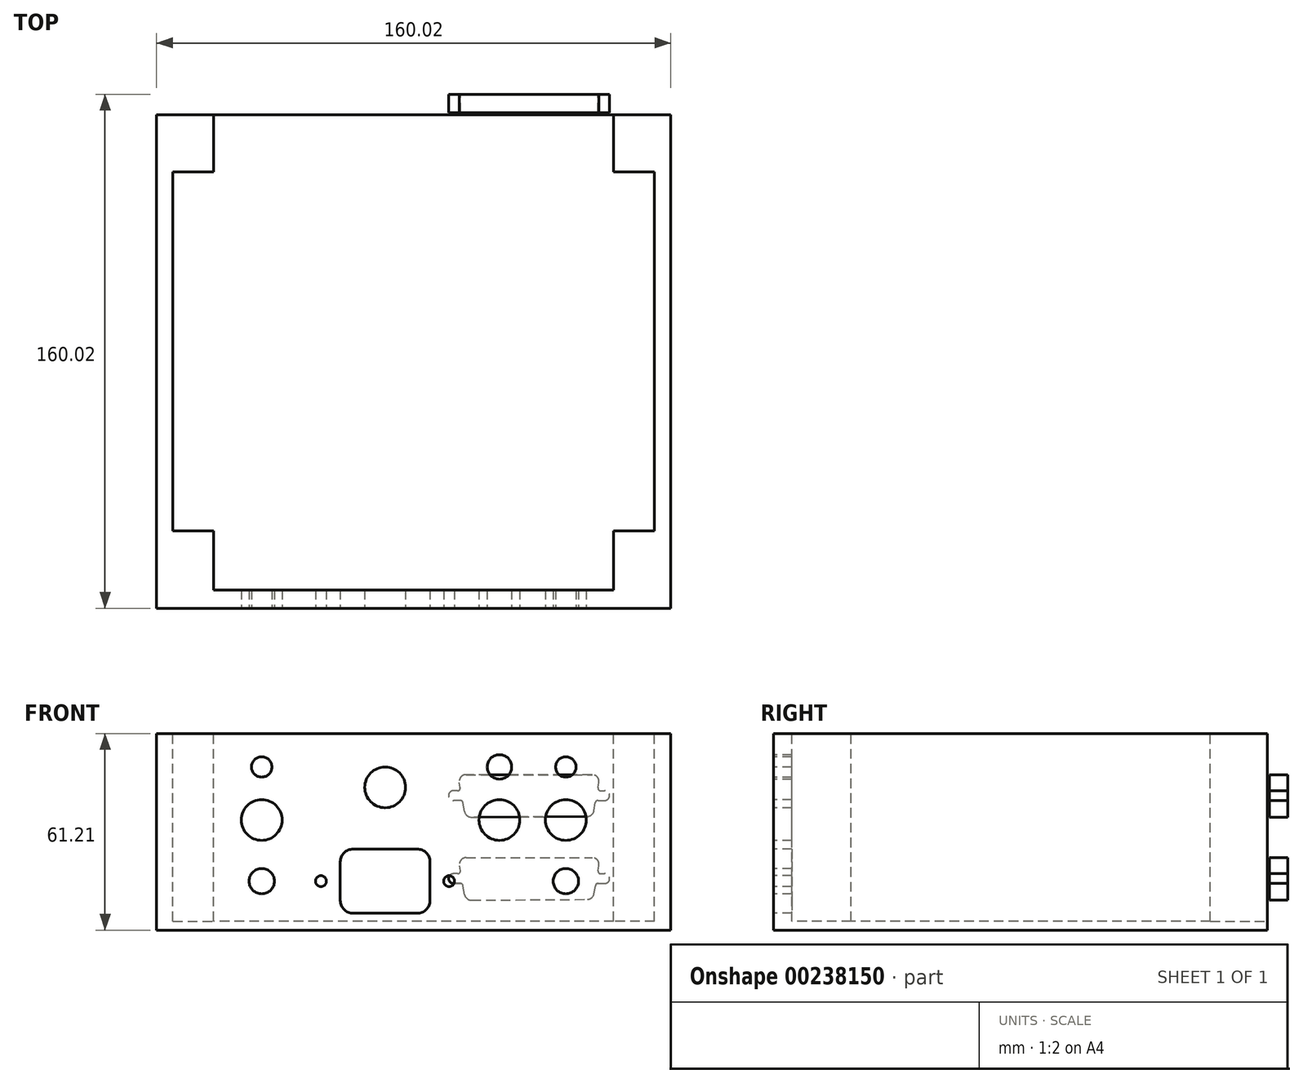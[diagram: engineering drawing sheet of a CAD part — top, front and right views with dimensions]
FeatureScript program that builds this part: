
annotation { "Feature Type Name" : "Feature", "Feature Type Description" : "" }
export const myFeature = defineFeature(function(context is Context, id is Id, definition is map)
    precondition{}
    {
        {
            var Q0;
            Q0=qCreatedBy(makeId("Top.planeOp"),FACE);
            var sketch = newSketch(context, id + "F0", { "sketchPlane" : qUnion([Q0])});
            skLineSegment(sketch, "E0.bottom", {"start": v(0, 0) * mm, "end": v(160.02, 0) * mm});
            skLineSegment(sketch, "E0.top", {"start": v(0, 160.02) * mm, "end": v(160.02, 160.02) * mm});
            skLineSegment(sketch, "E0.left", {"start": v(0, 0) * mm, "end": v(0, 160.02) * mm});
            skLineSegment(sketch, "E0.right", {"start": v(160.02, 0) * mm, "end": v(160.02, 160.02) * mm});
            skSolve(sketch);
        }
        {
            var Q0;
            Q0=makeQuery(id+"F0.imprint","IMPRINT",FACE,{"disambiguationData":[TD([[makeQuery(id+"F0.imprint","IMPRINT",EDGE,{"derivedFrom":sQuery(id+"F0.wireOp",EDGE,"E0.bottom")}),1.0]])]});
            extrude(context, id + "F1", {"entities" : qUnion([Q0]), "oppositeDirection" : true, "depth" : 61.2 * mm});
        }
        {
            var Q0;
            Q0=makeQuery(id+"F1.opExtrude","CAP_FACE",FACE,{"disambiguationData":[OSD([sQuery(id+"F0.wireOp",EDGE,"E0.bottom"),sQuery(id+"F0.wireOp",EDGE,"E0.top"),sQuery(id+"F0.wireOp",EDGE,"E0.left"),sQuery(id+"F0.wireOp",EDGE,"E0.right")])],"isStart":true});
            var sketch = newSketch(context, id + "F2", { "sketchPlane" : qUnion([Q0])});
            skLineSegment(sketch, "E1.bottom", {"start": v(5.08, 154.3) * mm, "end": v(154.94, 154.3) * mm});
            skLineSegment(sketch, "E1.top", {"start": v(5.08, 5.71) * mm, "end": v(154.94, 5.72) * mm});
            skLineSegment(sketch, "E1.left", {"start": v(5.08, 154.3) * mm, "end": v(5.08, 5.71) * mm});
            skLineSegment(sketch, "E1.right", {"start": v(154.94, 154.3) * mm, "end": v(154.94, 5.72) * mm});
            skLineSegment(sketch, "E2", {"start": v(5.08, 24.13) * mm, "end": v(17.78, 24.13) * mm});
            skLineSegment(sketch, "E3", {"start": v(17.78, 24.13) * mm, "end": v(17.78, 5.71) * mm});
            skLineSegment(sketch, "E4", {"start": v(154.94, 24.13) * mm, "end": v(142.24, 24.13) * mm});
            skLineSegment(sketch, "E5", {"start": v(142.24, 24.13) * mm, "end": v(142.24, 5.72) * mm});
            skLineSegment(sketch, "E6", {"start": v(5.08, 135.9) * mm, "end": v(17.78, 135.9) * mm});
            skLineSegment(sketch, "E7", {"start": v(17.78, 135.9) * mm, "end": v(17.78, 154.3) * mm});
            skLineSegment(sketch, "E8", {"start": v(154.94, 135.9) * mm, "end": v(142.24, 135.9) * mm});
            skLineSegment(sketch, "E9", {"start": v(142.24, 135.9) * mm, "end": v(142.24, 154.3) * mm});
            skSolve(sketch);
        }
        {
            var Q0;
            {var subQ3=sQuery(id+"F2.wireOp",EDGE,"E2");Q0=makeQuery(id+"F2.imprint","IMPRINT",FACE,{"disambiguationData":[TD([[makeQuery(id+"F2.imprint","IMPRINT",EDGE,{"derivedFrom":subQ3}),1.0]])]});}
            extrude(context, id + "F3", {"entities" : qUnion([Q0]), "operationType" : NewBodyOperationType.REMOVE, "oppositeDirection" : true, "depth" : 58.42 * mm});
        }
        {
            var Q0;
            Q0=makeQuery(id+"F1.opExtrude","SWEPT_FACE",FACE,{"disambiguationData":[OSD([sQuery(id+"F0.wireOp",EDGE,"E0.bottom")])]});
            var sketch = newSketch(context, id + "F4", { "sketchPlane" : qUnion([Q0])});
            skCircle(sketch, "E10", {"center": v(32.7, -45.97) * mm, "radius": 3.94 * mm});
            skCircle(sketch, "E11.1.0.0", {"center": v(127.34, -45.97) * mm, "radius": 3.94 * mm});
            skLineSegment(sketch, "E11.direction1", {"start": v(32.7, -45.97) * mm, "end": v(127.34, -45.97) * mm, "construction": true});
            skSolve(sketch);
        }
        {
            var Q0;
            Q0=makeQuery(id+"F4.imprint","IMPRINT",FACE,{"disambiguationData":[TD([[makeQuery(id+"F4.imprint","IMPRINT",EDGE,{"derivedFrom":sQuery(id+"F4.wireOp",EDGE,"E10")}),1.0]])]});
            var Q1;
            Q1=makeQuery(id+"F4.imprint","IMPRINT",FACE,{"disambiguationData":[TD([[makeQuery(id+"F4.imprint","IMPRINT",EDGE,{"derivedFrom":sQuery(id+"F4.wireOp",EDGE,"E11.1.0.0")}),1.0]])]});
            extrude(context, id + "F5", {"entities" : qUnion([Q0, Q1]), "operationType" : NewBodyOperationType.REMOVE, "oppositeDirection" : true, "depth" : 6.35 * mm});
        }
        {
            var Q0;
            Q0=makeQuery(id+"F1.opExtrude","SWEPT_FACE",FACE,{"disambiguationData":[OSD([sQuery(id+"F0.wireOp",EDGE,"E0.bottom")])]});
            var sketch = newSketch(context, id + "F6", { "sketchPlane" : qUnion([Q0])});
            skLineSegment(sketch, "E12.bottom", {"start": v(61.14, -35.98) * mm, "end": v(81.1, -35.98) * mm});
            skLineSegment(sketch, "E12.top", {"start": v(61.14, -55.97) * mm, "end": v(81.1, -55.97) * mm});
            skLineSegment(sketch, "E12.left", {"start": v(57.15, -39.97) * mm, "end": v(57.15, -51.98) * mm});
            skLineSegment(sketch, "E12.right", {"start": v(85.1, -39.97) * mm, "end": v(85.1, -51.98) * mm});
            skPoint(sketch, "E13.visualSharp", {"position": v(57.15, -35.98) * mm});
            skArc(sketch, "E13.filletArc", {"start": v(61.14, -35.98) * mm, "mid": v(58.32, -37.15) * mm, "end": v(57.15, -39.97) * mm});
            skPoint(sketch, "E14.visualSharp", {"position": v(57.15, -55.97) * mm});
            skArc(sketch, "E14.filletArc", {"start": v(57.15, -51.98) * mm, "mid": v(58.32, -54.8) * mm, "end": v(61.14, -55.97) * mm});
            skPoint(sketch, "E15.visualSharp", {"position": v(85.1, -55.97) * mm});
            skArc(sketch, "E15.filletArc", {"start": v(81.1, -55.97) * mm, "mid": v(83.92, -54.8) * mm, "end": v(85.1, -51.98) * mm});
            skPoint(sketch, "E16.visualSharp", {"position": v(85.1, -35.98) * mm});
            skArc(sketch, "E16.filletArc", {"start": v(85.1, -39.97) * mm, "mid": v(83.92, -37.15) * mm, "end": v(81.1, -35.98) * mm});
            skSolve(sketch);
        }
        {
            var Q0;
            Q0=makeQuery(id+"F6.imprint","IMPRINT",FACE,{"disambiguationData":[TD([[makeQuery(id+"F6.imprint","IMPRINT",EDGE,{"derivedFrom":sQuery(id+"F6.wireOp",EDGE,"E12.bottom")}),-1.0]])]});
            extrude(context, id + "F7", {"entities" : qUnion([Q0]), "operationType" : NewBodyOperationType.REMOVE, "oppositeDirection" : true, "depth" : 6.35 * mm});
        }
        {
            var Q0;
            Q0=makeQuery(id+"F1.opExtrude","SWEPT_FACE",FACE,{"disambiguationData":[OSD([sQuery(id+"F0.wireOp",EDGE,"E0.bottom")])]});
            var sketch = newSketch(context, id + "F8", { "sketchPlane" : qUnion([Q0])});
            skCircle(sketch, "E17", {"center": v(51.13, -45.97) * mm, "radius": 1.7 * mm});
            skCircle(sketch, "E18.1.0.0", {"center": v(91, -45.97) * mm, "radius": 1.7 * mm});
            skLineSegment(sketch, "E18.direction1", {"start": v(51.13, -45.97) * mm, "end": v(91, -45.97) * mm, "construction": true});
            skSolve(sketch);
        }
        {
            var Q0;
            Q0=makeQuery(id+"F8.imprint","IMPRINT",FACE,{"disambiguationData":[TD([[makeQuery(id+"F8.imprint","IMPRINT",EDGE,{"derivedFrom":sQuery(id+"F8.wireOp",EDGE,"E17")}),1.0]])]});
            var Q1;
            Q1=makeQuery(id+"F8.imprint","IMPRINT",FACE,{"disambiguationData":[TD([[makeQuery(id+"F8.imprint","IMPRINT",EDGE,{"derivedFrom":sQuery(id+"F8.wireOp",EDGE,"E18.1.0.0")}),1.0]])]});
            extrude(context, id + "F9", {"entities" : qUnion([Q0, Q1]), "operationType" : NewBodyOperationType.REMOVE, "oppositeDirection" : true, "depth" : 6.35 * mm});
        }
        {
            var Q0;
            Q0=makeQuery(id+"F1.opExtrude","SWEPT_FACE",FACE,{"disambiguationData":[OSD([sQuery(id+"F0.wireOp",EDGE,"E0.bottom")])]});
            var sketch = newSketch(context, id + "F10", { "sketchPlane" : qUnion([Q0])});
            skLineSegment(sketch, "E19.bottom", {"start": v(46.35, -34.98) * mm, "end": v(95.88, -34.98) * mm});
            skLineSegment(sketch, "E19.top", {"start": v(46.35, -56.97) * mm, "end": v(95.88, -56.97) * mm});
            skLineSegment(sketch, "E19.left", {"start": v(46.35, -34.98) * mm, "end": v(46.35, -56.97) * mm});
            skLineSegment(sketch, "E19.right", {"start": v(95.88, -34.98) * mm, "end": v(95.88, -56.97) * mm});
            skSolve(sketch);
        }
        {
            var Q0;
            Q0=makeQuery(id+"F10.imprint","IMPRINT",FACE,{"disambiguationData":[TD([[makeQuery(id+"F10.imprint","IMPRINT",EDGE,{"derivedFrom":sQuery(id+"F10.wireOp",EDGE,"E19.bottom")}),1.0]])]});
            var sketch = newSketch(context, id + "F11", { "sketchPlane" : qUnion([Q0])});
            skCircle(sketch, "E20", {"center": v(32.69, -26.92) * mm, "radius": 6.35 * mm});
            skCircle(sketch, "E21.1.0.0", {"center": v(127.33, -26.92) * mm, "radius": 6.35 * mm});
            skLineSegment(sketch, "E21.direction1", {"start": v(32.69, -26.92) * mm, "end": v(127.33, -26.92) * mm, "construction": true});
            skSolve(sketch);
        }
        {
            var Q0;
            Q0=makeQuery(id+"F11.imprint","IMPRINT",FACE,{"disambiguationData":[TD([[makeQuery(id+"F11.imprint","IMPRINT",EDGE,{"derivedFrom":sQuery(id+"F11.wireOp",EDGE,"E20")}),1.0]])]});
            var Q1;
            Q1=makeQuery(id+"F11.imprint","IMPRINT",FACE,{"disambiguationData":[TD([[makeQuery(id+"F11.imprint","IMPRINT",EDGE,{"derivedFrom":sQuery(id+"F11.wireOp",EDGE,"E21.1.0.0")}),1.0]])]});
            extrude(context, id + "F12", {"entities" : qUnion([Q0, Q1]), "operationType" : NewBodyOperationType.REMOVE, "oppositeDirection" : true, "depth" : 6.35 * mm});
        }
        {
            var Q0;
            Q0=makeQuery(id+"F10.imprint","IMPRINT",FACE,{"disambiguationData":[TD([[makeQuery(id+"F10.imprint","IMPRINT",EDGE,{"derivedFrom":sQuery(id+"F10.wireOp",EDGE,"E19.bottom")}),1.0]])]});
            var sketch = newSketch(context, id + "F13", { "sketchPlane" : qUnion([Q0])});
            skCircle(sketch, "E22", {"center": v(32.69, -10.41) * mm, "radius": 3.18 * mm});
            skCircle(sketch, "E23.1.0.0", {"center": v(127.33, -10.41) * mm, "radius": 3.18 * mm});
            skLineSegment(sketch, "E23.direction1", {"start": v(32.69, -10.41) * mm, "end": v(127.33, -10.41) * mm, "construction": true});
            skSolve(sketch);
        }
        {
            var Q0;
            Q0=qSketchRegion(id+"F13",true);
            extrude(context, id + "F14", {"entities" : qUnion([Q0]), "operationType" : NewBodyOperationType.REMOVE, "oppositeDirection" : true, "depth" : 6.35 * mm});
        }
        {
            var Q0;
            Q0=makeQuery(id+"F10.imprint","IMPRINT",FACE,{"disambiguationData":[TD([[makeQuery(id+"F10.imprint","IMPRINT",EDGE,{"derivedFrom":sQuery(id+"F10.wireOp",EDGE,"E19.bottom")}),1.0]])]});
            var sketch = newSketch(context, id + "F15", { "sketchPlane" : qUnion([Q0])});
            skCircle(sketch, "E24", {"center": v(71.12, -16.76) * mm, "radius": 6.35 * mm});
            skSolve(sketch);
        }
        {
            var Q0;
            Q0=makeQuery(id+"F15.imprint","IMPRINT",FACE,{"disambiguationData":[TD([[makeQuery(id+"F15.imprint","IMPRINT",EDGE,{"derivedFrom":sQuery(id+"F15.wireOp",EDGE,"E24")}),1.0]])]});
            extrude(context, id + "F16", {"entities" : qUnion([Q0]), "operationType" : NewBodyOperationType.REMOVE, "oppositeDirection" : true, "depth" : 6.35 * mm});
        }
        {
            var Q0;
            Q0=makeQuery(id+"F10.imprint","IMPRINT",FACE,{"disambiguationData":[TD([[makeQuery(id+"F10.imprint","IMPRINT",EDGE,{"derivedFrom":sQuery(id+"F10.wireOp",EDGE,"E19.bottom")}),1.0]])]});
            var sketch = newSketch(context, id + "F17", { "sketchPlane" : qUnion([Q0])});
            skCircle(sketch, "E25", {"center": v(106.68, -26.92) * mm, "radius": 6.35 * mm});
            skSolve(sketch);
        }
        {
            var Q0;
            Q0=qSketchRegion(id+"F17",true);
            extrude(context, id + "F18", {"entities" : qUnion([Q0]), "operationType" : NewBodyOperationType.REMOVE, "oppositeDirection" : true, "depth" : 6.35 * mm});
        }
        {
            var Q0;
            Q0=makeQuery(id+"F10.imprint","IMPRINT",FACE,{"disambiguationData":[TD([[makeQuery(id+"F10.imprint","IMPRINT",EDGE,{"derivedFrom":sQuery(id+"F10.wireOp",EDGE,"E19.bottom")}),1.0]])]});
            var sketch = newSketch(context, id + "F19", { "sketchPlane" : qUnion([Q0])});
            skCircle(sketch, "E26", {"center": v(106.68, -10.41) * mm, "radius": 3.81 * mm});
            skSolve(sketch);
        }
        {
            var Q0;
            Q0=qSketchRegion(id+"F19",true);
            extrude(context, id + "F20", {"entities" : qUnion([Q0]), "operationType" : NewBodyOperationType.REMOVE, "oppositeDirection" : true, "depth" : 6.35 * mm});
        }
        {
            var Q0;
            Q0=makeQuery(id+"F1.opExtrude","SWEPT_FACE",FACE,{"disambiguationData":[OSD([sQuery(id+"F0.wireOp",EDGE,"E0.top")])]});
            var sketch = newSketch(context, id + "F21", { "sketchPlane" : qUnion([Q0])});
            skSolve(sketch);
        }
        {
            var Q0;
            {var subQ0=sQuery(id+"F0.wireOp",EDGE,"E0.top");Q0=makeQuery(id+"F21.imprint","IMPRINT",FACE,{"disambiguationData":[TD([[makeQuery(id+"F21.imprint","IMPRINT",EDGE,{"derivedFrom":makeQuery(id+"F1.opExtrude","CAP_EDGE",EDGE,{"disambiguationData":[OSD([subQ0])],"isStart":true})}),1.0]])]});}
            var sketch = newSketch(context, id + "F22", { "sketchPlane" : qUnion([Q0])});
            skLineSegment(sketch, "E27", {"start": v(-140.97, -45.17) * mm, "end": v(-139.45, -45.17) * mm, "construction": true});
            skArc(sketch, "E28", {"start": v(-139.45, -46.7) * mm, "mid": v(-140.97, -45.17) * mm, "end": v(-139.45, -43.65) * mm});
            skLineSegment(sketch, "E29", {"start": v(-90.88, -45.17) * mm, "end": v(-92.4, -45.17) * mm, "construction": true});
            skArc(sketch, "E30", {"start": v(-92.4, -43.65) * mm, "mid": v(-90.88, -45.17) * mm, "end": v(-92.4, -46.7) * mm});
            skLineSegment(sketch, "E31", {"start": v(-135.56, -38.66) * mm, "end": v(-96.31, -38.66) * mm});
            skLineSegment(sketch, "E32", {"start": v(-137.64, -41.13) * mm, "end": v(-137.36, -42.7) * mm});
            skLineSegment(sketch, "E33", {"start": v(-94.24, -41.13) * mm, "end": v(-94.51, -42.7) * mm});
            skLineSegment(sketch, "E34", {"start": v(-134.03, -51.66) * mm, "end": v(-97.92, -51.9) * mm});
            skLineSegment(sketch, "E35", {"start": v(-92.4, -43.65) * mm, "end": v(-93.71, -43.65) * mm});
            skLineSegment(sketch, "E36", {"start": v(-92.4, -46.7) * mm, "end": v(-94.54, -46.7) * mm});
            skLineSegment(sketch, "E37", {"start": v(-139.45, -43.65) * mm, "end": v(-138.16, -43.65) * mm});
            skLineSegment(sketch, "E38", {"start": v(-139.45, -46.7) * mm, "end": v(-137.34, -46.7) * mm});
            skLineSegment(sketch, "E39.trimOffspring", {"start": v(-136.54, -47.37) * mm, "end": v(-136.09, -49.92) * mm});
            skLineSegment(sketch, "E40.trimOffspring", {"start": v(-95.34, -47.37) * mm, "end": v(-95.83, -50.15) * mm});
            skPoint(sketch, "E41.visualSharp", {"position": v(-135.78, -51.65) * mm});
            skArc(sketch, "E41.filletArc", {"start": v(-136.09, -49.92) * mm, "mid": v(-135.37, -51.17) * mm, "end": v(-134.03, -51.66) * mm});
            skPoint(sketch, "E42.visualSharp", {"position": v(-96.14, -51.9) * mm});
            skArc(sketch, "E42.filletArc", {"start": v(-97.92, -51.9) * mm, "mid": v(-96.55, -51.4) * mm, "end": v(-95.83, -50.15) * mm});
            skPoint(sketch, "E43.visualSharp", {"position": v(-93.8, -38.66) * mm});
            skArc(sketch, "E43.filletArc", {"start": v(-94.24, -41.13) * mm, "mid": v(-94.7, -39.41) * mm, "end": v(-96.31, -38.66) * mm});
            skPoint(sketch, "E44.visualSharp", {"position": v(-138.07, -38.66) * mm});
            skArc(sketch, "E44.filletArc", {"start": v(-135.56, -38.66) * mm, "mid": v(-137.18, -39.41) * mm, "end": v(-137.64, -41.13) * mm});
            skPoint(sketch, "E45.visualSharp", {"position": v(-136.66, -46.7) * mm});
            skArc(sketch, "E45.filletArc", {"start": v(-136.54, -47.37) * mm, "mid": v(-136.82, -46.89) * mm, "end": v(-137.34, -46.7) * mm});
            skPoint(sketch, "E46.visualSharp", {"position": v(-137.2, -43.65) * mm});
            skArc(sketch, "E46.filletArc", {"start": v(-138.16, -43.65) * mm, "mid": v(-137.54, -43.36) * mm, "end": v(-137.36, -42.7) * mm});
            skPoint(sketch, "E47.visualSharp", {"position": v(-94.68, -43.65) * mm});
            skArc(sketch, "E47.filletArc", {"start": v(-94.51, -42.7) * mm, "mid": v(-94.34, -43.36) * mm, "end": v(-93.71, -43.65) * mm});
            skPoint(sketch, "E48.visualSharp", {"position": v(-95.22, -46.7) * mm});
            skArc(sketch, "E48.filletArc", {"start": v(-94.54, -46.7) * mm, "mid": v(-95.06, -46.89) * mm, "end": v(-95.34, -47.37) * mm});
            skLineSegment(sketch, "E49", {"start": v(-140.94, -19.32) * mm, "end": v(-139.42, -19.32) * mm, "construction": true});
            skArc(sketch, "E50", {"start": v(-139.42, -20.85) * mm, "mid": v(-140.94, -19.32) * mm, "end": v(-139.42, -17.8) * mm});
            skLineSegment(sketch, "E51", {"start": v(-90.85, -19.32) * mm, "end": v(-92.38, -19.32) * mm, "construction": true});
            skArc(sketch, "E52", {"start": v(-92.38, -17.8) * mm, "mid": v(-90.85, -19.32) * mm, "end": v(-92.38, -20.85) * mm});
            skLineSegment(sketch, "E53", {"start": v(-135.54, -12.8) * mm, "end": v(-96.29, -12.8) * mm});
            skLineSegment(sketch, "E54", {"start": v(-137.61, -15.28) * mm, "end": v(-137.34, -16.85) * mm});
            skLineSegment(sketch, "E55", {"start": v(-94.21, -15.28) * mm, "end": v(-94.49, -16.85) * mm});
            skLineSegment(sketch, "E56", {"start": v(-134, -25.82) * mm, "end": v(-97.9, -26.04) * mm});
            skLineSegment(sketch, "E57", {"start": v(-92.38, -17.8) * mm, "end": v(-93.69, -17.8) * mm});
            skLineSegment(sketch, "E58", {"start": v(-92.38, -20.85) * mm, "end": v(-94.51, -20.85) * mm});
            skLineSegment(sketch, "E59", {"start": v(-139.42, -17.8) * mm, "end": v(-138.14, -17.8) * mm});
            skLineSegment(sketch, "E60", {"start": v(-139.42, -20.85) * mm, "end": v(-137.31, -20.85) * mm});
            skLineSegment(sketch, "E61.trimOffspring", {"start": v(-136.51, -21.52) * mm, "end": v(-136.06, -24.07) * mm});
            skLineSegment(sketch, "E62.trimOffspring", {"start": v(-95.31, -21.52) * mm, "end": v(-95.8, -24.3) * mm});
            skPoint(sketch, "E63.visualSharp", {"position": v(-135.76, -25.8) * mm});
            skArc(sketch, "E63.filletArc", {"start": v(-136.06, -24.07) * mm, "mid": v(-135.35, -25.32) * mm, "end": v(-134, -25.82) * mm});
            skPoint(sketch, "E64.visualSharp", {"position": v(-96.11, -26.05) * mm});
            skArc(sketch, "E64.filletArc", {"start": v(-97.9, -26.04) * mm, "mid": v(-96.53, -25.55) * mm, "end": v(-95.8, -24.3) * mm});
            skPoint(sketch, "E65.visualSharp", {"position": v(-93.78, -12.8) * mm});
            skArc(sketch, "E65.filletArc", {"start": v(-94.21, -15.28) * mm, "mid": v(-94.67, -13.56) * mm, "end": v(-96.29, -12.8) * mm});
            skPoint(sketch, "E66.visualSharp", {"position": v(-138.05, -12.8) * mm});
            skArc(sketch, "E66.filletArc", {"start": v(-135.54, -12.8) * mm, "mid": v(-137.15, -13.56) * mm, "end": v(-137.61, -15.28) * mm});
            skPoint(sketch, "E67.visualSharp", {"position": v(-136.63, -20.85) * mm});
            skArc(sketch, "E67.filletArc", {"start": v(-136.51, -21.52) * mm, "mid": v(-136.79, -21.04) * mm, "end": v(-137.31, -20.85) * mm});
            skPoint(sketch, "E68.visualSharp", {"position": v(-137.17, -17.8) * mm});
            skArc(sketch, "E68.filletArc", {"start": v(-138.14, -17.8) * mm, "mid": v(-137.51, -17.51) * mm, "end": v(-137.34, -16.85) * mm});
            skPoint(sketch, "E69.visualSharp", {"position": v(-94.66, -17.8) * mm});
            skArc(sketch, "E69.filletArc", {"start": v(-94.49, -16.85) * mm, "mid": v(-94.3, -17.51) * mm, "end": v(-93.69, -17.8) * mm});
            skPoint(sketch, "E70.visualSharp", {"position": v(-95.2, -20.85) * mm});
            skArc(sketch, "E70.filletArc", {"start": v(-94.51, -20.85) * mm, "mid": v(-95.03, -21.04) * mm, "end": v(-95.31, -21.52) * mm});
            skSolve(sketch);
        }
        {
            var Q0;
            Q0=makeQuery(id+"F22.imprint","IMPRINT",FACE,{"disambiguationData":[TD([[makeQuery(id+"F22.imprint","IMPRINT",EDGE,{"derivedFrom":sQuery(id+"F22.wireOp",EDGE,"E50")}),-1.0]])]});
            var Q1;
            Q1=makeQuery(id+"F22.imprint","IMPRINT",FACE,{"disambiguationData":[TD([[makeQuery(id+"F22.imprint","IMPRINT",EDGE,{"derivedFrom":sQuery(id+"F22.wireOp",EDGE,"E28")}),-1.0]])]});
            extrude(context, id + "F23", {"entities" : qUnion([Q0, Q1]), "operationType" : NewBodyOperationType.REMOVE, "oppositeDirection" : true, "depth" : 6.35 * mm});
        }
        {
            var Q0;
            {var subQ0=sQuery(id+"F0.wireOp",EDGE,"E0.top");Q0=makeQuery(id+"F21.imprint","IMPRINT",FACE,{"disambiguationData":[TD([[makeQuery(id+"F21.imprint","IMPRINT",EDGE,{"derivedFrom":makeQuery(id+"F1.opExtrude","CAP_EDGE",EDGE,{"disambiguationData":[OSD([subQ0])],"isStart":true})}),1.0]])]});}
            var sketch = newSketch(context, id + "F24", { "sketchPlane" : qUnion([Q0])});
            skLineSegment(sketch, "E71.bottom", {"start": v(-52.07, -38.99) * mm, "end": v(-39.37, -38.99) * mm});
            skLineSegment(sketch, "E71.top", {"start": v(-52.07, -51.69) * mm, "end": v(-39.37, -51.69) * mm});
            skLineSegment(sketch, "E71.left", {"start": v(-52.07, -38.99) * mm, "end": v(-52.07, -51.69) * mm});
            skLineSegment(sketch, "E71.right", {"start": v(-39.37, -38.99) * mm, "end": v(-39.37, -51.69) * mm});
            skCircle(sketch, "E72", {"center": v(-60.7, -45.34) * mm, "radius": 1.83 * mm});
            skCircle(sketch, "E73.1.0.0", {"center": v(-30.7, -45.34) * mm, "radius": 1.83 * mm});
            skLineSegment(sketch, "E73.direction1", {"start": v(-60.7, -45.34) * mm, "end": v(-30.7, -45.34) * mm, "construction": true});
            skSolve(sketch);
        }
        {
            var Q0;
            Q0=makeQuery(id+"F24.imprint","IMPRINT",FACE,{"disambiguationData":[TD([[makeQuery(id+"F24.imprint","IMPRINT",EDGE,{"derivedFrom":sQuery(id+"F24.wireOp",EDGE,"E71.bottom")}),-1.0]])]});
            var Q1;
            Q1=makeQuery(id+"F24.imprint","IMPRINT",FACE,{"disambiguationData":[TD([[makeQuery(id+"F24.imprint","IMPRINT",EDGE,{"derivedFrom":sQuery(id+"F24.wireOp",EDGE,"E72")}),1.0]])]});
            var Q2;
            Q2=makeQuery(id+"F24.imprint","IMPRINT",FACE,{"disambiguationData":[TD([[makeQuery(id+"F24.imprint","IMPRINT",EDGE,{"derivedFrom":sQuery(id+"F24.wireOp",EDGE,"E73.1.0.0")}),1.0]])]});
            extrude(context, id + "F25", {"entities" : qUnion([Q0, Q1, Q2]), "operationType" : NewBodyOperationType.REMOVE, "oppositeDirection" : true, "depth" : 6.35 * mm});
        }
    });
